# Revit family: EV-ATSB 40.63.80 Fan ATS Panel
name_source: partatom
category: Generic Models
units: mm (PartAtom-declared; Revit-internal decimal feet)

## family parameters
Always vertical = No
Can host rebar = No
Cut with Voids When Loaded = No
OmniClass Number = 23.40.00.00
OmniClass Title = Equipment and Furnishings
Part Type = Normal
Room Calculation Point = No
Round Connector Dimension = Use Diameter
Shared = No
Work Plane-Based = Yes

## types (1)
- Controls
    BIMObject Category_2 = Controls
    BIMobject category = Electrical
    Colour = Light Grey RAL 7035
    Connection cable = 40A & 63A upto 16mm2. 80A upto 25mm2
    Cost = 0 $
    Current consumption = 40A - 63A - 80A
    Default Elevation = 1000 mm  [stored 3.28084 ft]
    Depth = 300 mm
    Design country = UK
    Edition number = 1
    Finish = Mild Steel
    Green Tag = Easivent Text
    Height = 642 mm
    IFC Classification = Controller
    IP rating = IP55
    Installation instructions = To be be wall mounted
    Keynote = Can be located outdoors. Cable connection from bottom of panel
    Manufacturer = Easivent
    Manufacturer URL = http://easivent.co.uk
    Manufacturer country = UK
    Manufacturer name = Easivent
    Material Main = Casing - Main Box
    Model = EV-ATSB 40 / EV-ATSB 63 / EV-ATSB 80
    NBS Reference Code = 16-16-15
    NBS Reference Description = Control Panels
    Name of the object = EV-ATSB 40/63/80
    Nominal height = 642
    Nominal width = 800
    Notes = Please note this product may be amended without prior notification
    Product SKU = ST4 3160
    Product data URL = Please enquire
    Product family = Control Panel
    Product group = Controls
    SerialNumber = 0
    Size = 800x300x642mm (W x D x H)
    Switch-on-duration_2 = Sensor/ Switch Controlled
    TagNumber = 0
    Technical description = Please enquire for electrical schematics
    To be ordered separately = All switches and controls
    Type Comments = Automatic Transfer Switch (ATS) suitable with smoke ventilation systems.
    Uniclass 2.0 Code = Pr_16_16_15
    Uniclass 2.0 Description = Control Panels
    Voltage = 400V
    WarrantyDuration = 12
    WarrantyStartDate = From items dispatch
    Weight Net (Kg) = Please enquire
    Width = 800
    switch-on-duration = Atomatic transfer

note: [stored X ft] marks values corroborated as IEEE doubles in the binary element streams (Revit-internal decimal feet)

## geometry (parser evidence)
native form markers: Sweep x8
no freeform markers — native parametric forms only
